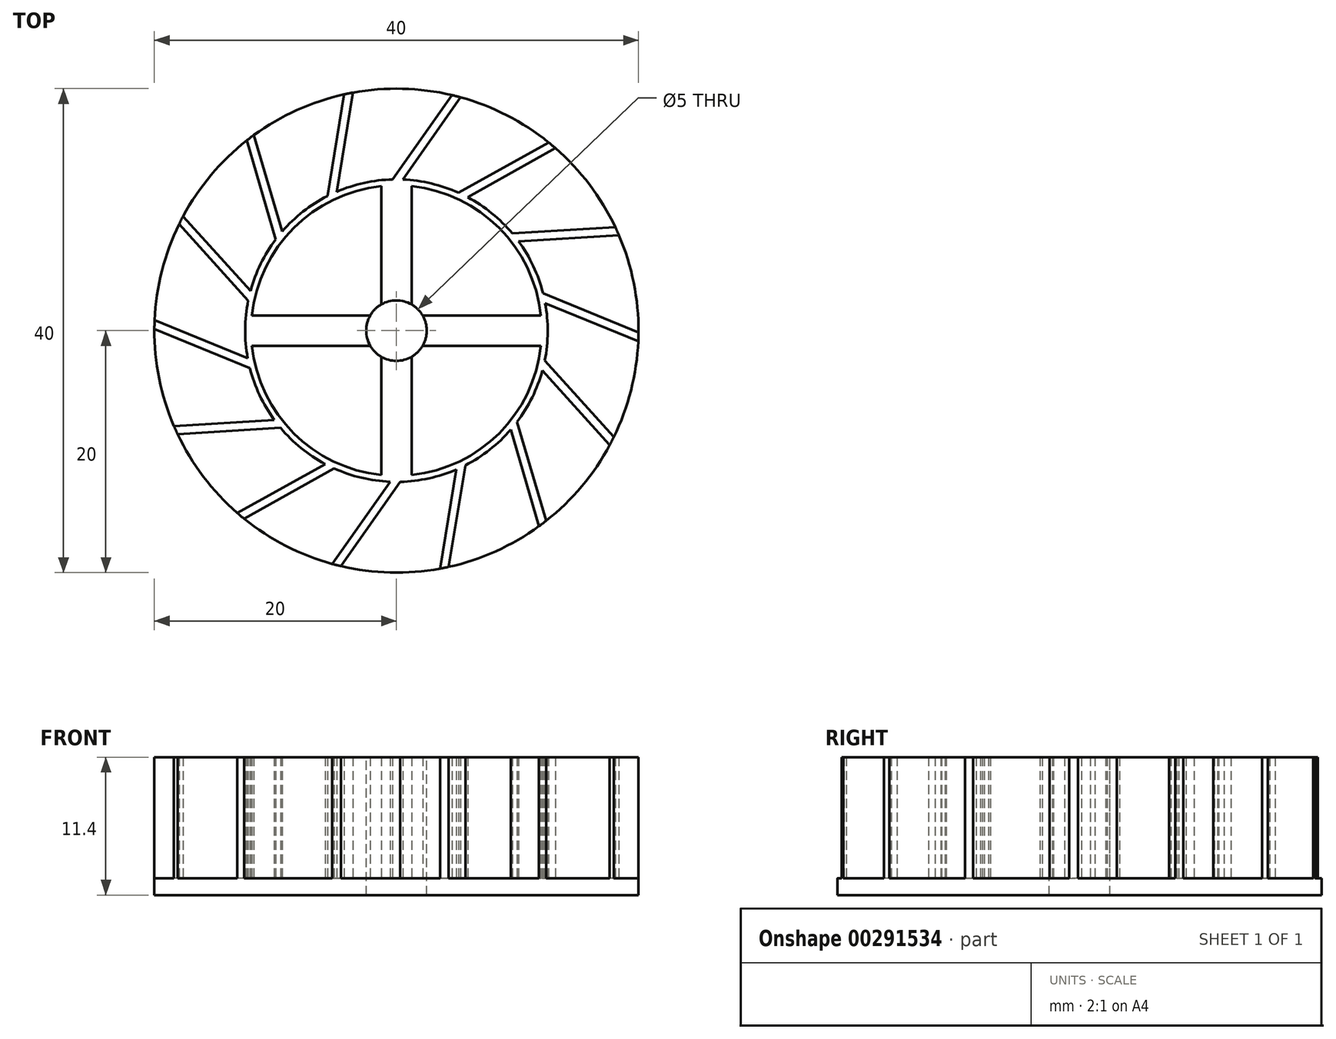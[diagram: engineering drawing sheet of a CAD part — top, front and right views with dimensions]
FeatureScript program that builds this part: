
annotation { "Feature Type Name" : "Feature", "Feature Type Description" : "" }
export const myFeature = defineFeature(function(context is Context, id is Id, definition is map)
    precondition{}
    {
        {
            var Q0;
            Q0=qCreatedBy(makeId("Top.planeOp"),FACE);
            var sketch = newSketch(context, id + "F0", { "sketchPlane" : qUnion([Q0])});
            skCircle(sketch, "E0", {"center": v(0, 0) * mm, "radius": 20 * mm});
            skSolve(sketch);
        }
        {
            var Q0;
            Q0=makeQuery(id+"F0.imprint","IMPRINT",FACE,{"disambiguationData":[TD([[makeQuery(id+"F0.imprint","IMPRINT",EDGE,{"derivedFrom":sQuery(id+"F0.wireOp",EDGE,"E0")}),1.0]])]});
            var Q1;
            Q1=sQuery(id+"F0.wireOp",EDGE,"E0");
            extrude(context, id + "F1", {"entities" : qUnion([Q0]), "surfaceEntities" : qUnion([Q1]), "depth" : 1.4 * mm});
        }
        {
            var Q0;
            Q0=makeQuery(id+"F1.opExtrude","CAP_FACE",FACE,{"disambiguationData":[OSD([sQuery(id+"F0.wireOp",EDGE,"E0")])],"isStart":false});
            var sketch = newSketch(context, id + "F2", { "sketchPlane" : qUnion([Q0])});
            skCircle(sketch, "E1", {"center": v(0, 0) * mm, "radius": 12.5 * mm});
            skLineSegment(sketch, "E2", {"start": v(-5.7, 11.12) * mm, "end": v(-4.32, 19.53) * mm});
            skLineSegment(sketch, "E3", {"start": v(-4.95, 11.48) * mm, "end": v(-3.6, 19.67) * mm});
            skLineSegment(sketch, "E4.1.0", {"start": v(-9.96, 7.55) * mm, "end": v(-12.36, 15.72) * mm});
            skLineSegment(sketch, "E4.1.1", {"start": v(-9.44, 8.2) * mm, "end": v(-11.78, 16.17) * mm});
            skLineSegment(sketch, "E4.2.0", {"start": v(-12.25, 2.48) * mm, "end": v(-17.96, 8.8) * mm});
            skLineSegment(sketch, "E4.2.1", {"start": v(-12.06, 3.3) * mm, "end": v(-17.62, 9.46) * mm});
            skLineSegment(sketch, "E4.3.0", {"start": v(-12.11, -3.09) * mm, "end": v(-20, 0.14) * mm});
            skLineSegment(sketch, "E4.3.1", {"start": v(-12.3, -2.27) * mm, "end": v(-19.98, 0.87) * mm});
            skLineSegment(sketch, "E4.4.0", {"start": v(-9.57, -8.04) * mm, "end": v(-18.08, -8.56) * mm});
            skLineSegment(sketch, "E4.4.1", {"start": v(-10.1, -7.38) * mm, "end": v(-18.38, -7.88) * mm});
            skLineSegment(sketch, "E4.5.0", {"start": v(-5.14, -11.4) * mm, "end": v(-12.58, -15.55) * mm});
            skLineSegment(sketch, "E4.5.1", {"start": v(-5.9, -11.02) * mm, "end": v(-13.14, -15.08) * mm});
            skLineSegment(sketch, "E4.6.0", {"start": v(0.31, -12.5) * mm, "end": v(-4.58, -19.47) * mm});
            skLineSegment(sketch, "E4.6.1", {"start": v(-0.52, -12.49) * mm, "end": v(-5.3, -19.29) * mm});
            skLineSegment(sketch, "E4.7.0", {"start": v(5.7, -11.12) * mm, "end": v(4.32, -19.53) * mm});
            skLineSegment(sketch, "E4.7.1", {"start": v(4.95, -11.48) * mm, "end": v(3.6, -19.67) * mm});
            skLineSegment(sketch, "E4.8.0", {"start": v(9.96, -7.55) * mm, "end": v(12.36, -15.72) * mm});
            skLineSegment(sketch, "E4.8.1", {"start": v(9.44, -8.2) * mm, "end": v(11.78, -16.17) * mm});
            skLineSegment(sketch, "E4.9.0", {"start": v(12.25, -2.48) * mm, "end": v(17.96, -8.8) * mm});
            skLineSegment(sketch, "E4.9.1", {"start": v(12.06, -3.3) * mm, "end": v(17.62, -9.46) * mm});
            skLineSegment(sketch, "E4.10.0", {"start": v(12.11, 3.09) * mm, "end": v(20, -0.14) * mm});
            skLineSegment(sketch, "E4.10.1", {"start": v(12.3, 2.27) * mm, "end": v(19.98, -0.87) * mm});
            skLineSegment(sketch, "E4.11.0", {"start": v(9.57, 8.04) * mm, "end": v(18.08, 8.56) * mm});
            skLineSegment(sketch, "E4.11.1", {"start": v(10.1, 7.38) * mm, "end": v(18.38, 7.88) * mm});
            skLineSegment(sketch, "E4.12.0", {"start": v(5.14, 11.4) * mm, "end": v(12.58, 15.55) * mm});
            skLineSegment(sketch, "E4.12.1", {"start": v(5.9, 11.02) * mm, "end": v(13.14, 15.08) * mm});
            skLineSegment(sketch, "E4.13.0", {"start": v(-0.31, 12.5) * mm, "end": v(4.58, 19.47) * mm});
            skLineSegment(sketch, "E4.13.1", {"start": v(0.52, 12.49) * mm, "end": v(5.3, 19.29) * mm});
            skCircle(sketch, "E5", {"center": v(0, 0) * mm, "radius": 12 * mm});
            skCircle(sketch, "E6", {"center": v(0, 0) * mm, "radius": 2.5 * mm});
            skLineSegment(sketch, "E7", {"start": v(-1.25, 11.93) * mm, "end": v(-1.25, 2.17) * mm});
            skLineSegment(sketch, "E8", {"start": v(2.17, 1.25) * mm, "end": v(11.93, 1.25) * mm});
            skLineSegment(sketch, "E9", {"start": v(2.17, -1.25) * mm, "end": v(11.93, -1.25) * mm});
            skLineSegment(sketch, "E10", {"start": v(-2.17, 1.25) * mm, "end": v(-11.93, 1.25) * mm});
            skLineSegment(sketch, "E11", {"start": v(-2.17, -1.25) * mm, "end": v(-11.93, -1.25) * mm});
            skLineSegment(sketch, "E12", {"start": v(1.25, 11.93) * mm, "end": v(1.25, 2.17) * mm});
            skLineSegment(sketch, "E13", {"start": v(1.25, -2.17) * mm, "end": v(1.25, -11.93) * mm});
            skLineSegment(sketch, "E14", {"start": v(-1.25, -2.17) * mm, "end": v(-1.25, -11.93) * mm});
            skSolve(sketch);
        }
        {
            var Q0;
            {var subQ0=sQuery(id+"F2.wireOp",EDGE,"E2");Q0=makeQuery(id+"F2.imprint","IMPRINT",FACE,{"disambiguationData":[TD([[makeQuery(id+"F2.imprint","IMPRINT",EDGE,{"derivedFrom":subQ0}),-1.0]])]});}
            var Q1;
            {var subQ0=sQuery(id+"F2.wireOp",EDGE,"E4.13.0");Q1=makeQuery(id+"F2.imprint","IMPRINT",FACE,{"disambiguationData":[TD([[makeQuery(id+"F2.imprint","IMPRINT",EDGE,{"derivedFrom":subQ0}),-1.0]])]});}
            var Q2;
            {var subQ0=sQuery(id+"F2.wireOp",EDGE,"E4.12.0");Q2=makeQuery(id+"F2.imprint","IMPRINT",FACE,{"disambiguationData":[TD([[makeQuery(id+"F2.imprint","IMPRINT",EDGE,{"derivedFrom":subQ0}),-1.0]])]});}
            var Q3;
            {var subQ0=sQuery(id+"F2.wireOp",EDGE,"E4.11.0");Q3=makeQuery(id+"F2.imprint","IMPRINT",FACE,{"disambiguationData":[TD([[makeQuery(id+"F2.imprint","IMPRINT",EDGE,{"derivedFrom":subQ0}),-1.0]])]});}
            var Q4;
            {var subQ0=sQuery(id+"F2.wireOp",EDGE,"E4.10.0");Q4=makeQuery(id+"F2.imprint","IMPRINT",FACE,{"disambiguationData":[TD([[makeQuery(id+"F2.imprint","IMPRINT",EDGE,{"derivedFrom":subQ0}),-1.0]])]});}
            var Q5;
            {var subQ0=sQuery(id+"F2.wireOp",EDGE,"E4.9.0");Q5=makeQuery(id+"F2.imprint","IMPRINT",FACE,{"disambiguationData":[TD([[makeQuery(id+"F2.imprint","IMPRINT",EDGE,{"derivedFrom":subQ0}),-1.0]])]});}
            var Q6;
            {var subQ0=sQuery(id+"F2.wireOp",EDGE,"E4.8.0");Q6=makeQuery(id+"F2.imprint","IMPRINT",FACE,{"disambiguationData":[TD([[makeQuery(id+"F2.imprint","IMPRINT",EDGE,{"derivedFrom":subQ0}),-1.0]])]});}
            var Q7;
            {var subQ0=sQuery(id+"F2.wireOp",EDGE,"E4.7.0");Q7=makeQuery(id+"F2.imprint","IMPRINT",FACE,{"disambiguationData":[TD([[makeQuery(id+"F2.imprint","IMPRINT",EDGE,{"derivedFrom":subQ0}),-1.0]])]});}
            var Q8;
            {var subQ0=sQuery(id+"F2.wireOp",EDGE,"E4.6.0");Q8=makeQuery(id+"F2.imprint","IMPRINT",FACE,{"disambiguationData":[TD([[makeQuery(id+"F2.imprint","IMPRINT",EDGE,{"derivedFrom":subQ0}),-1.0]])]});}
            var Q9;
            {var subQ0=sQuery(id+"F2.wireOp",EDGE,"E4.5.0");Q9=makeQuery(id+"F2.imprint","IMPRINT",FACE,{"disambiguationData":[TD([[makeQuery(id+"F2.imprint","IMPRINT",EDGE,{"derivedFrom":subQ0}),-1.0]])]});}
            var Q10;
            {var subQ0=sQuery(id+"F2.wireOp",EDGE,"E4.4.0");Q10=makeQuery(id+"F2.imprint","IMPRINT",FACE,{"disambiguationData":[TD([[makeQuery(id+"F2.imprint","IMPRINT",EDGE,{"derivedFrom":subQ0}),-1.0]])]});}
            var Q11;
            {var subQ0=sQuery(id+"F2.wireOp",EDGE,"E4.3.0");Q11=makeQuery(id+"F2.imprint","IMPRINT",FACE,{"disambiguationData":[TD([[makeQuery(id+"F2.imprint","IMPRINT",EDGE,{"derivedFrom":subQ0}),-1.0]])]});}
            var Q12;
            {var subQ0=sQuery(id+"F2.wireOp",EDGE,"E4.2.0");Q12=makeQuery(id+"F2.imprint","IMPRINT",FACE,{"disambiguationData":[TD([[makeQuery(id+"F2.imprint","IMPRINT",EDGE,{"derivedFrom":subQ0}),-1.0]])]});}
            var Q13;
            {var subQ0=sQuery(id+"F2.wireOp",EDGE,"E4.1.0");Q13=makeQuery(id+"F2.imprint","IMPRINT",FACE,{"disambiguationData":[TD([[makeQuery(id+"F2.imprint","IMPRINT",EDGE,{"derivedFrom":subQ0}),-1.0]])]});}
            extrude(context, id + "F3", {"entities" : qUnion([Q0, Q1, Q2, Q3, Q4, Q5, Q6, Q7, Q8, Q9, Q10, Q11, Q12, Q13]), "operationType" : NewBodyOperationType.ADD, "depth" : 10 * mm});
        }
        {
            var Q0;
            Q0=makeQuery(id+"F2.imprint","IMPRINT",FACE,{"disambiguationData":[TD([[makeQuery(id+"F2.imprint","IMPRINT",EDGE,{"derivedFrom":sQuery(id+"F2.wireOp",EDGE,"E5")}),-1.0]])]});
            extrude(context, id + "F4", {"entities" : qUnion([Q0]), "operationType" : NewBodyOperationType.ADD, "depth" : 10 * mm});
        }
        {
            var Q0;
            {var subQ0=sQuery(id+"F2.wireOp",EDGE,"E6");var subQ5=makeQuery(id+"F2.imprint","INTERSECT",VERTEX,{"derivedFrom":[subQ0,sQuery(id+"F2.wireOp",EDGE,"E8")]});Q0=makeQuery(id+"F2.imprint","IMPRINT",FACE,{"disambiguationData":[TD([[makeQuery(id+"F2.imprint","IMPRINT",EDGE,{"disambiguationData":[TD([[subQ5,-1.0]])],"derivedFrom":subQ0}),1.0]])]});}
            extrude(context, id + "F5", {"entities" : qUnion([Q0]), "operationType" : NewBodyOperationType.REMOVE, "oppositeDirection" : true, "depth" : 25.4 * mm});
        }
        {
            var Q0;
            {var subQ0=sQuery(id+"F2.wireOp",EDGE,"E7");Q0=makeQuery(id+"F2.imprint","IMPRINT",FACE,{"disambiguationData":[TD([[makeQuery(id+"F2.imprint","IMPRINT",EDGE,{"derivedFrom":subQ0}),1.0]])]});}
            var Q1;
            {var subQ0=sQuery(id+"F2.wireOp",EDGE,"E8");Q1=makeQuery(id+"F2.imprint","IMPRINT",FACE,{"disambiguationData":[TD([[makeQuery(id+"F2.imprint","IMPRINT",EDGE,{"derivedFrom":subQ0}),-1.0]])]});}
            var Q2;
            {var subQ0=sQuery(id+"F2.wireOp",EDGE,"E13");Q2=makeQuery(id+"F2.imprint","IMPRINT",FACE,{"disambiguationData":[TD([[makeQuery(id+"F2.imprint","IMPRINT",EDGE,{"derivedFrom":subQ0}),-1.0]])]});}
            var Q3;
            {var subQ0=sQuery(id+"F2.wireOp",EDGE,"E10");Q3=makeQuery(id+"F2.imprint","IMPRINT",FACE,{"disambiguationData":[TD([[makeQuery(id+"F2.imprint","IMPRINT",EDGE,{"derivedFrom":subQ0}),1.0]])]});}
            extrude(context, id + "F6", {"entities" : qUnion([Q0, Q1, Q2, Q3]), "operationType" : NewBodyOperationType.ADD, "depth" : 10 * mm});
        }
    });
